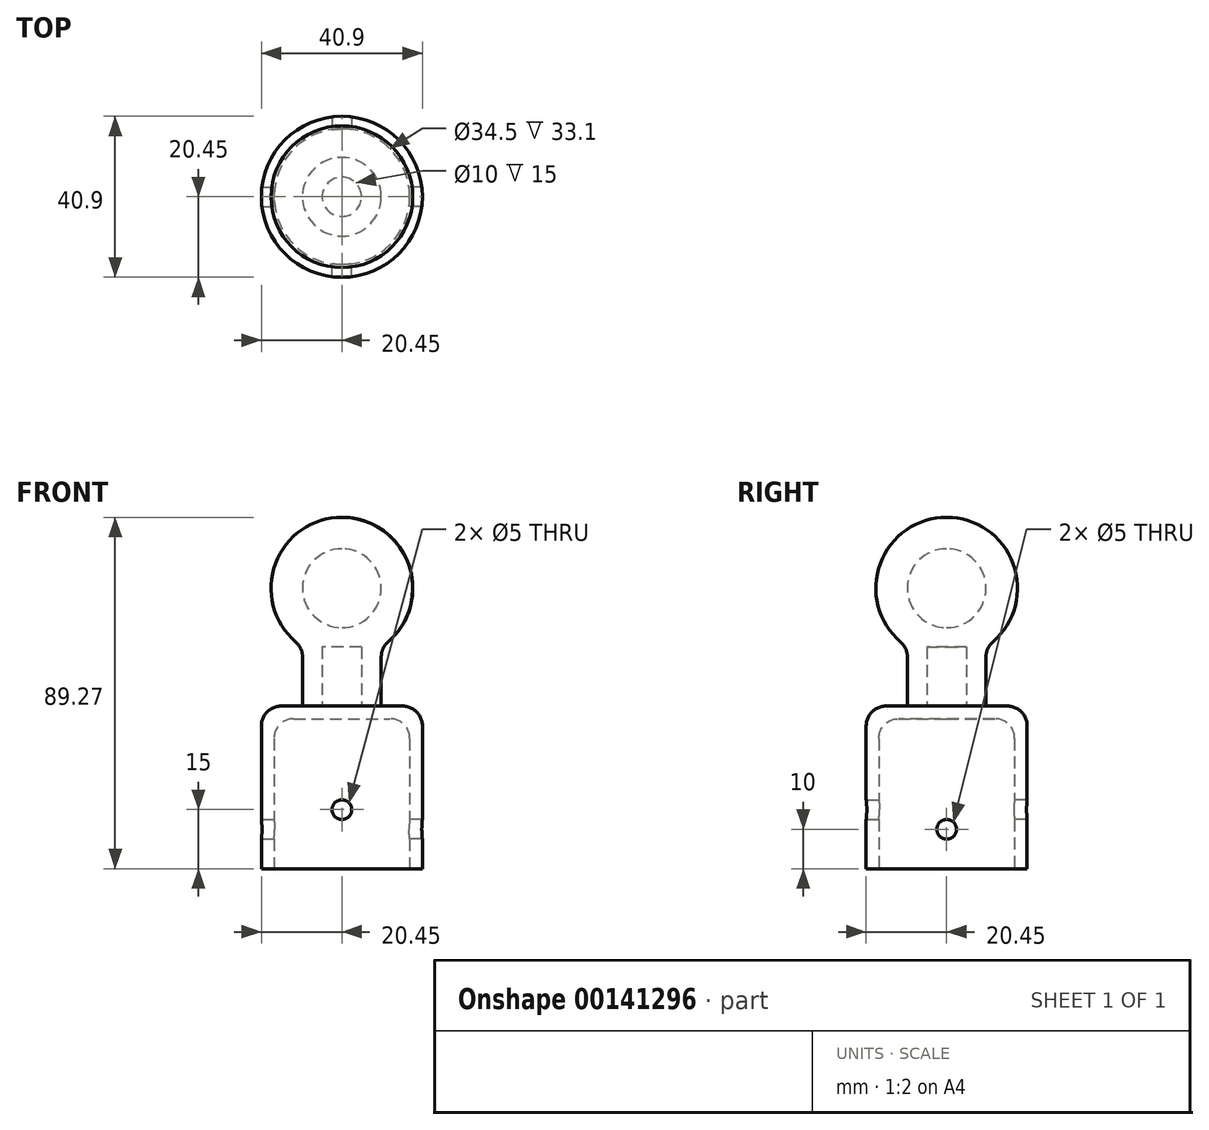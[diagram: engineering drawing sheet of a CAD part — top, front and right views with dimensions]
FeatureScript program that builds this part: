
annotation { "Feature Type Name" : "Feature", "Feature Type Description" : "" }
export const myFeature = defineFeature(function(context is Context, id is Id, definition is map)
    precondition{}
    {
        {
            var Q0;
            Q0=qCreatedBy(makeId("Front.planeOp"),FACE);
            var sketch = newSketch(context, id + "F0", { "sketchPlane" : qUnion([Q0])});
            skLineSegment(sketch, "E0", {"start": v(17.25, 0) * mm, "end": v(17.25, 33.1) * mm});
            skLineSegment(sketch, "E1", {"start": v(12.25, 38.1) * mm, "end": v(0, 38.1) * mm});
            skLineSegment(sketch, "E2", {"start": v(0, 38.1) * mm, "end": v(0, 41.3) * mm});
            skLineSegment(sketch, "E3", {"start": v(0, 41.3) * mm, "end": v(20.45, 41.3) * mm});
            skLineSegment(sketch, "E4", {"start": v(20.45, 41.3) * mm, "end": v(20.45, 0) * mm});
            skLineSegment(sketch, "E5", {"start": v(20.45, 0) * mm, "end": v(17.25, 0) * mm});
            skPoint(sketch, "E6.visualSharp", {"position": v(17.25, 38.1) * mm});
            skArc(sketch, "E6.filletArc", {"start": v(17.25, 33.1) * mm, "mid": v(15.79, 36.64) * mm, "end": v(12.25, 38.1) * mm});
            skSolve(sketch);
        }
        {
            var Q0;
            Q0=qSketchRegion(id+"F0",true);
            var Q1;
            Q1=sQuery(id+"F0.wireOp",EDGE,"E2");
            revolve(context, id + "F1", {"entities" : qUnion([Q0]), "axis" : qUnion([Q1]), "revolveType" : RevolveType.FULL});
        }
        {
            var Q0;
            Q0=makeQuery(id+"F1.opRevolve","SWEPT_FACE",FACE,{"disambiguationData":[OSD([sQuery(id+"F0.wireOp",EDGE,"E3")])]});
            var sketch = newSketch(context, id + "F2", { "sketchPlane" : qUnion([Q0])});
            skCircle(sketch, "E7", {"center": v(0, 0) * mm, "radius": 10 * mm});
            skCircle(sketch, "E8", {"center": v(0, 0) * mm, "radius": 5 * mm});
            skSolve(sketch);
        }
        {
            var Q0;
            Q0 = qSketchRegion(id + "F2", true);
            extrude(context, id + "F3", {"entities" : qUnion([Q0]), "operationType" : NewBodyOperationType.ADD, "depth" : 15 * mm});
        }
        {
            var Q0;
            Q0=qCreatedBy(makeId("Front.planeOp"),FACE);
            var sketch = newSketch(context, id + "F4", { "sketchPlane" : qUnion([Q0])});
            skArc(sketch, "E9", {"start": v(10, 56.3) * mm, "mid": v(17.22, 76.5) * mm, "end": v(0, 89.27) * mm});
            skArc(sketch, "E10", {"start": v(0, 81.27) * mm, "mid": v(10, 71.27) * mm, "end": v(0, 61.27) * mm});
            skLineSegment(sketch, "E11", {"start": v(0, 61.27) * mm, "end": v(0, 56.3) * mm});
            skLineSegment(sketch, "E12", {"start": v(0, 56.3) * mm, "end": v(10, 56.3) * mm});
            skLineSegment(sketch, "E13", {"start": v(0, 89.27) * mm, "end": v(0, 81.27) * mm});
            skSolve(sketch);
        }
        {
            var Q0;
            Q0 = qSketchRegion(id + "F4", true);
            var Q1;
            Q1=sQuery(id+"F4.wireOp",EDGE,"E13");
            revolve(context, id + "F5", {"operationType" : NewBodyOperationType.ADD, "entities" : qUnion([Q0]), "axis" : qUnion([Q1]), "revolveType" : RevolveType.FULL});
        }
        {
            var Q0;
            Q0=makeQuery(id+"F5.boolean.opBoolean","MERGE",EDGE,{"derivedFrom":[makeQuery(id+"F3.opExtrude","CAP_EDGE",EDGE,{"disambiguationData":[OSD([sQuery(id+"F2.wireOp",EDGE,"E7")])],"isStart":false}),makeQuery(id+"F5.opRevolve","SWEPT_EDGE",EDGE,{"disambiguationData":[OSD([sQuery(id+"F4.wireOp",EDGE,"E9"),sQuery(id+"F4.wireOp",EDGE,"E12")])]})]});
            var Q1;
            Q1=makeQuery(id+"F1.opRevolve","SWEPT_EDGE",EDGE,{"disambiguationData":[OSD([sQuery(id+"F0.wireOp",EDGE,"E3"),sQuery(id+"F0.wireOp",EDGE,"E4")])]});
            var Q2;
            Q2=makeQuery(id+"F3.opExtrude","CAP_EDGE",EDGE,{"disambiguationData":[OSD([sQuery(id+"F2.wireOp",EDGE,"E7")])],"isStart":true});
            fillet(context, id + "F6", {"entities" : qUnion([Q0, Q1, Q2]), "radius" : 5 * mm, "tangentPropagation" : true, "allowEdgeOverflow" : false});
        }
        {
            var Q0;
            Q0=qCreatedBy(makeId("Front.planeOp"),FACE);
            var sketch = newSketch(context, id + "F7", { "sketchPlane" : qUnion([Q0])});
            skLineSegment(sketch, "E14.bottom", {"start": v(2.5, 12.5) * mm, "end": v(-2.5, 12.5) * mm});
            skLineSegment(sketch, "E14.top", {"start": v(2.5, 17.5) * mm, "end": v(-2.5, 17.5) * mm});
            skLineSegment(sketch, "E14.left", {"start": v(2.5, 12.5) * mm, "end": v(2.5, 17.5) * mm});
            skLineSegment(sketch, "E14.right", {"start": v(-2.5, 12.5) * mm, "end": v(-2.5, 17.5) * mm});
            skPoint(sketch, "E14.middle", {"position": v(0, 15) * mm});
            skSolve(sketch);
        }
        {
            var Q0;
            Q0 = qSketchRegion(id + "F7", true);
            extrude(context, id + "F8", {"entities" : qUnion([Q0]), "operationType" : NewBodyOperationType.REMOVE, "endBound" : BoundingType.SYMMETRIC, "depth" : 50 * mm});
        }
        {
            var Q0;
            Q0=qCreatedBy(makeId("Right.planeOp"),FACE);
            var sketch = newSketch(context, id + "F9", { "sketchPlane" : qUnion([Q0])});
            skLineSegment(sketch, "E15.bottom", {"start": v(2.5, 7.5) * mm, "end": v(-2.5, 7.5) * mm});
            skLineSegment(sketch, "E15.top", {"start": v(2.5, 12.5) * mm, "end": v(-2.5, 12.5) * mm});
            skLineSegment(sketch, "E15.left", {"start": v(2.5, 7.5) * mm, "end": v(2.5, 12.5) * mm});
            skLineSegment(sketch, "E15.right", {"start": v(-2.5, 7.5) * mm, "end": v(-2.5, 12.5) * mm});
            skPoint(sketch, "E15.middle", {"position": v(0, 10) * mm});
            skSolve(sketch);
        }
        {
            var Q0;
            Q0 = qSketchRegion(id + "F9", true);
            extrude(context, id + "F10", {"entities" : qUnion([Q0]), "operationType" : NewBodyOperationType.REMOVE, "endBound" : BoundingType.SYMMETRIC, "oppositeDirection" : true, "depth" : 50 * mm});
        }
        {
            var Q0;
            Q0=makeQuery(id+"F10.boolean.opBoolean","COPY",EDGE,{"disambiguationData":[OD(1.0)],"derivedFrom":makeQuery(id+"F10.opExtrude","SWEPT_EDGE",EDGE,{"disambiguationData":[OSD([sQuery(id+"F9.wireOp",EDGE,"E15.top"),sQuery(id+"F9.wireOp",EDGE,"E15.right")])]})});
            var Q1;
            Q1=makeQuery(id+"F10.boolean.opBoolean","COPY",EDGE,{"disambiguationData":[OD(1.0)],"derivedFrom":makeQuery(id+"F10.opExtrude","SWEPT_EDGE",EDGE,{"disambiguationData":[OSD([sQuery(id+"F9.wireOp",EDGE,"E15.bottom"),sQuery(id+"F9.wireOp",EDGE,"E15.right")])]})});
            var Q2;
            Q2=makeQuery(id+"F10.boolean.opBoolean","COPY",EDGE,{"disambiguationData":[OD(1.0)],"derivedFrom":makeQuery(id+"F10.opExtrude","SWEPT_EDGE",EDGE,{"disambiguationData":[OSD([sQuery(id+"F9.wireOp",EDGE,"E15.bottom"),sQuery(id+"F9.wireOp",EDGE,"E15.left")])]})});
            var Q3;
            Q3=makeQuery(id+"F10.boolean.opBoolean","COPY",EDGE,{"disambiguationData":[OD(1.0)],"derivedFrom":makeQuery(id+"F10.opExtrude","SWEPT_EDGE",EDGE,{"disambiguationData":[OSD([sQuery(id+"F9.wireOp",EDGE,"E15.top"),sQuery(id+"F9.wireOp",EDGE,"E15.left")])]})});
            var Q4;
            Q4=makeQuery(id+"F8.boolean.opBoolean","COPY",EDGE,{"disambiguationData":[OD(1.0)],"derivedFrom":makeQuery(id+"F8.opExtrude","SWEPT_EDGE",EDGE,{"disambiguationData":[OSD([sQuery(id+"F7.wireOp",EDGE,"E14.top"),sQuery(id+"F7.wireOp",EDGE,"E14.right")])]})});
            var Q5;
            Q5=makeQuery(id+"F8.boolean.opBoolean","COPY",EDGE,{"disambiguationData":[OD(1.0)],"derivedFrom":makeQuery(id+"F8.opExtrude","SWEPT_EDGE",EDGE,{"disambiguationData":[OSD([sQuery(id+"F7.wireOp",EDGE,"E14.bottom"),sQuery(id+"F7.wireOp",EDGE,"E14.right")])]})});
            var Q6;
            Q6=makeQuery(id+"F8.boolean.opBoolean","COPY",EDGE,{"disambiguationData":[OD(1.0)],"derivedFrom":makeQuery(id+"F8.opExtrude","SWEPT_EDGE",EDGE,{"disambiguationData":[OSD([sQuery(id+"F7.wireOp",EDGE,"E14.bottom"),sQuery(id+"F7.wireOp",EDGE,"E14.left")])]})});
            var Q7;
            Q7=makeQuery(id+"F8.boolean.opBoolean","COPY",EDGE,{"disambiguationData":[OD(1.0)],"derivedFrom":makeQuery(id+"F8.opExtrude","SWEPT_EDGE",EDGE,{"disambiguationData":[OSD([sQuery(id+"F7.wireOp",EDGE,"E14.top"),sQuery(id+"F7.wireOp",EDGE,"E14.left")])]})});
            var Q8;
            Q8=makeQuery(id+"F10.boolean.opBoolean","COPY",EDGE,{"disambiguationData":[OD(0.0)],"derivedFrom":makeQuery(id+"F10.opExtrude","SWEPT_EDGE",EDGE,{"disambiguationData":[OSD([sQuery(id+"F9.wireOp",EDGE,"E15.bottom"),sQuery(id+"F9.wireOp",EDGE,"E15.right")])]})});
            var Q9;
            Q9=makeQuery(id+"F10.boolean.opBoolean","COPY",EDGE,{"disambiguationData":[OD(0.0)],"derivedFrom":makeQuery(id+"F10.opExtrude","SWEPT_EDGE",EDGE,{"disambiguationData":[OSD([sQuery(id+"F9.wireOp",EDGE,"E15.top"),sQuery(id+"F9.wireOp",EDGE,"E15.left")])]})});
            var Q10;
            Q10=makeQuery(id+"F10.boolean.opBoolean","COPY",EDGE,{"disambiguationData":[OD(0.0)],"derivedFrom":makeQuery(id+"F10.opExtrude","SWEPT_EDGE",EDGE,{"disambiguationData":[OSD([sQuery(id+"F9.wireOp",EDGE,"E15.bottom"),sQuery(id+"F9.wireOp",EDGE,"E15.left")])]})});
            var Q11;
            Q11=makeQuery(id+"F10.boolean.opBoolean","COPY",EDGE,{"disambiguationData":[OD(0.0)],"derivedFrom":makeQuery(id+"F10.opExtrude","SWEPT_EDGE",EDGE,{"disambiguationData":[OSD([sQuery(id+"F9.wireOp",EDGE,"E15.top"),sQuery(id+"F9.wireOp",EDGE,"E15.right")])]})});
            var Q12;
            Q12=makeQuery(id+"F8.boolean.opBoolean","COPY",EDGE,{"disambiguationData":[OD(0.0)],"derivedFrom":makeQuery(id+"F8.opExtrude","SWEPT_EDGE",EDGE,{"disambiguationData":[OSD([sQuery(id+"F7.wireOp",EDGE,"E14.bottom"),sQuery(id+"F7.wireOp",EDGE,"E14.left")])]})});
            var Q13;
            Q13=makeQuery(id+"F8.boolean.opBoolean","COPY",EDGE,{"disambiguationData":[OD(0.0)],"derivedFrom":makeQuery(id+"F8.opExtrude","SWEPT_EDGE",EDGE,{"disambiguationData":[OSD([sQuery(id+"F7.wireOp",EDGE,"E14.top"),sQuery(id+"F7.wireOp",EDGE,"E14.left")])]})});
            var Q14;
            Q14=makeQuery(id+"F8.boolean.opBoolean","COPY",EDGE,{"disambiguationData":[OD(0.0)],"derivedFrom":makeQuery(id+"F8.opExtrude","SWEPT_EDGE",EDGE,{"disambiguationData":[OSD([sQuery(id+"F7.wireOp",EDGE,"E14.bottom"),sQuery(id+"F7.wireOp",EDGE,"E14.right")])]})});
            var Q15;
            Q15=makeQuery(id+"F8.boolean.opBoolean","COPY",EDGE,{"disambiguationData":[OD(0.0)],"derivedFrom":makeQuery(id+"F8.opExtrude","SWEPT_EDGE",EDGE,{"disambiguationData":[OSD([sQuery(id+"F7.wireOp",EDGE,"E14.top"),sQuery(id+"F7.wireOp",EDGE,"E14.right")])]})});
            fillet(context, id + "F11", {"entities" : qUnion([Q0, Q1, Q2, Q3, Q4, Q5, Q6, Q7, Q8, Q9, Q10, Q11, Q12, Q13, Q14, Q15]), "radius" : 2.5 * mm, "tangentPropagation" : true, "allowEdgeOverflow" : false});
        }
    });
